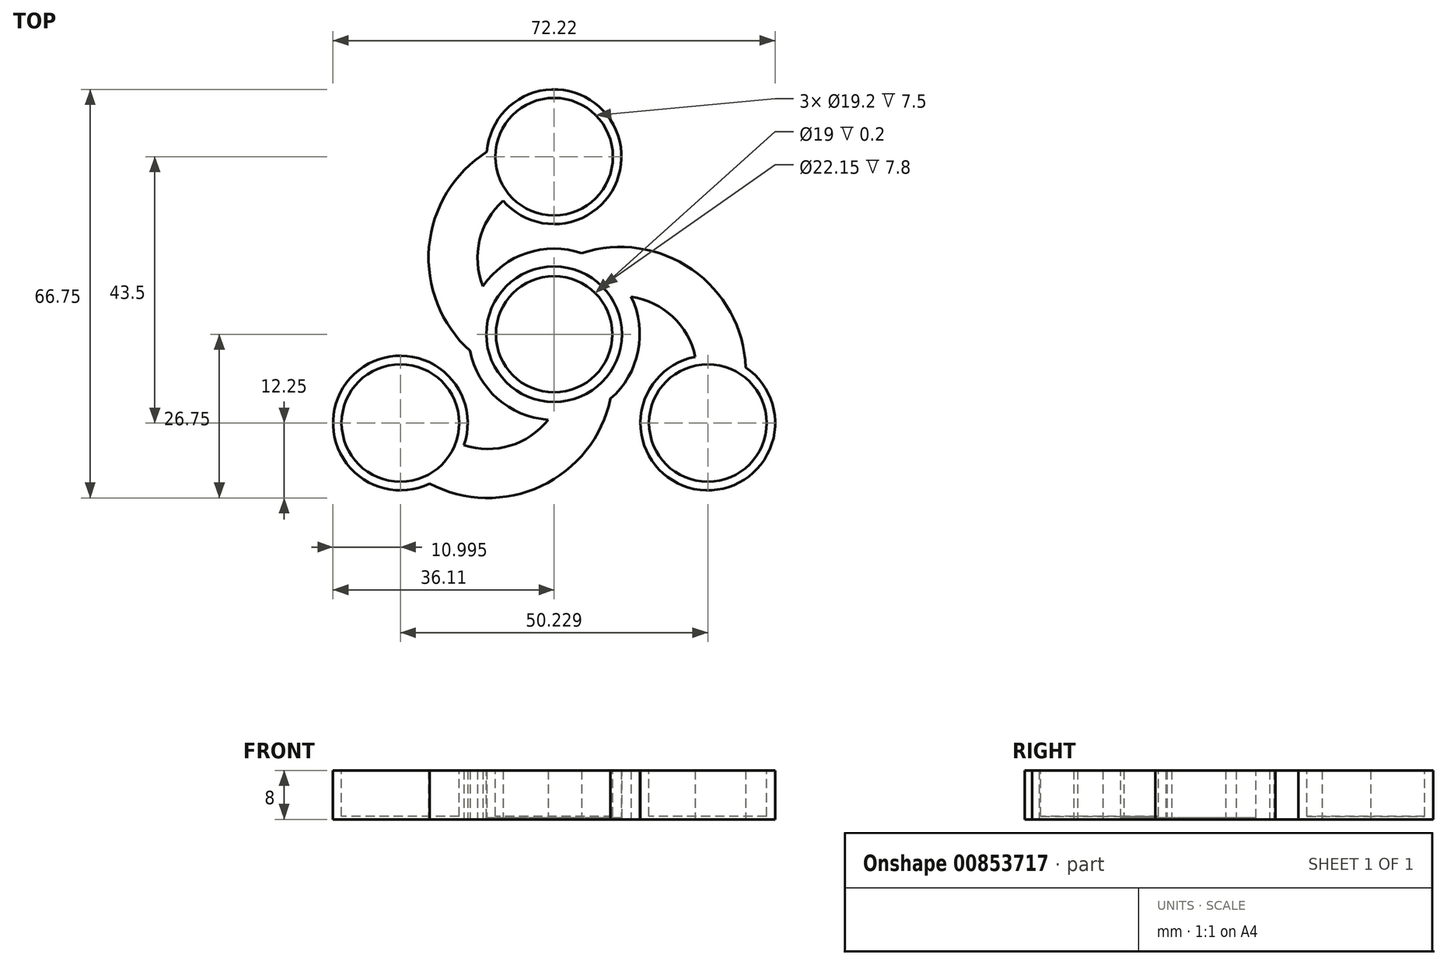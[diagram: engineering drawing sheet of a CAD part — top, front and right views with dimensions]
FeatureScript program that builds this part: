
annotation { "Feature Type Name" : "Feature", "Feature Type Description" : "" }
export const myFeature = defineFeature(function(context is Context, id is Id, definition is map)
    precondition{}
    {
        {
            var Q0;
            Q0=qCreatedBy(makeId("Top.planeOp"),FACE);
            var sketch = newSketch(context, id + "F0", { "sketchPlane" : qUnion([Q0])});
            skCircle(sketch, "E0", {"center": v(0, 0) * mm, "radius": 14 * mm});
            skLineSegment(sketch, "E1", {"start": v(0, 0) * mm, "end": v(0, 25) * mm, "construction": true});
            skArc(sketch, "E2", {"start": v(0, 25) * mm, "mid": v(-12.5, 12.5) * mm, "end": v(0, 0) * mm});
            skArc(sketch, "E3.0", {"start": v(0, 33) * mm, "mid": v(-20.5, 12.5) * mm, "end": v(0, -8) * mm});
            skLineSegment(sketch, "E4", {"start": v(0, 25) * mm, "end": v(0, 33) * mm, "construction": true});
            skCircle(sketch, "E5", {"center": v(0, 29) * mm, "radius": 11 * mm});
            skArc(sketch, "E6.1.0", {"start": v(-21.65, -12.5) * mm, "mid": v(-4.58, -17.08) * mm, "end": v(0, 0) * mm});
            skArc(sketch, "E6.1.1", {"start": v(-28.58, -16.5) * mm, "mid": v(-0.58, -24) * mm, "end": v(6.93, 4) * mm});
            skCircle(sketch, "E6.1.2", {"center": v(-25.11, -14.5) * mm, "radius": 11 * mm});
            skArc(sketch, "E6.2.0", {"start": v(21.65, -12.5) * mm, "mid": v(17.08, 4.58) * mm, "end": v(0, 0) * mm});
            skArc(sketch, "E6.2.1", {"start": v(28.58, -16.5) * mm, "mid": v(21.08, 11.5) * mm, "end": v(-6.93, 4) * mm});
            skCircle(sketch, "E6.2.2", {"center": v(25.11, -14.5) * mm, "radius": 11 * mm});
            skSolve(sketch);
        }
        {
            var Q0;
            {var subQ0=sQuery(id+"F0.wireOp",EDGE,"E6.1.1");var subQ1=sQuery(id+"F0.wireOp",EDGE,"E0");var subQ2=makeQuery(id+"F0.imprint","INTERSECT",VERTEX,{"derivedFrom":[subQ1,subQ0]});Q0=makeQuery(id+"F0.imprint","IMPRINT",FACE,{"disambiguationData":[TD([[makeQuery(id+"F0.imprint","IMPRINT",EDGE,{"disambiguationData":[TD([[subQ2,1.0]])],"derivedFrom":subQ1}),-1.0]])]});}
            var Q1;
            {var subQ0=sQuery(id+"F0.wireOp",EDGE,"E0");var subQ1=makeQuery(id+"F0.imprint","INTERSECT",VERTEX,{"derivedFrom":[subQ0,sQuery(id+"F0.wireOp",EDGE,"E6.1.1")]});Q1=makeQuery(id+"F0.imprint","IMPRINT",FACE,{"disambiguationData":[TD([[makeQuery(id+"F0.imprint","IMPRINT",EDGE,{"disambiguationData":[TD([[subQ1,1.0]])],"derivedFrom":subQ0}),1.0]])]});}
            var Q2;
            {var subQ0=sQuery(id+"F0.wireOp",EDGE,"E0");var subQ1=makeQuery(id+"F0.imprint","INTERSECT",VERTEX,{"derivedFrom":[subQ0,sQuery(id+"F0.wireOp",EDGE,"E3.0")]});Q2=makeQuery(id+"F0.imprint","IMPRINT",FACE,{"disambiguationData":[TD([[makeQuery(id+"F0.imprint","IMPRINT",EDGE,{"disambiguationData":[TD([[subQ1,1.0]])],"derivedFrom":subQ0}),1.0]])]});}
            var Q3;
            {var subQ0=sQuery(id+"F0.wireOp",EDGE,"E6.1.2");var subQ1=makeQuery(id+"F0.imprint","INTERSECT",VERTEX,{"derivedFrom":[sQuery(id+"F0.wireOp",EDGE,"E6.1.0"),subQ0]});Q3=makeQuery(id+"F0.imprint","IMPRINT",FACE,{"disambiguationData":[TD([[makeQuery(id+"F0.imprint","IMPRINT",EDGE,{"disambiguationData":[TD([[subQ1,1.0]])],"derivedFrom":subQ0}),1.0]])]});}
            var Q4;
            {var subQ0=sQuery(id+"F0.wireOp",EDGE,"E6.2.2");var subQ1=makeQuery(id+"F0.imprint","INTERSECT",VERTEX,{"derivedFrom":[sQuery(id+"F0.wireOp",EDGE,"E6.2.0"),subQ0]});Q4=makeQuery(id+"F0.imprint","IMPRINT",FACE,{"disambiguationData":[TD([[makeQuery(id+"F0.imprint","IMPRINT",EDGE,{"disambiguationData":[TD([[subQ1,1.0]])],"derivedFrom":subQ0}),1.0]])]});}
            var Q5;
            {var subQ0=sQuery(id+"F0.wireOp",EDGE,"E6.2.1");var subQ1=sQuery(id+"F0.wireOp",EDGE,"E0");var subQ2=makeQuery(id+"F0.imprint","INTERSECT",VERTEX,{"derivedFrom":[subQ1,subQ0]});Q5=makeQuery(id+"F0.imprint","IMPRINT",FACE,{"disambiguationData":[TD([[makeQuery(id+"F0.imprint","IMPRINT",EDGE,{"disambiguationData":[TD([[subQ2,1.0]])],"derivedFrom":subQ1}),-1.0]])]});}
            var Q6;
            {var subQ0=sQuery(id+"F0.wireOp",EDGE,"E0");var subQ1=makeQuery(id+"F0.imprint","INTERSECT",VERTEX,{"derivedFrom":[subQ0,sQuery(id+"F0.wireOp",EDGE,"E6.2.1")]});Q6=makeQuery(id+"F0.imprint","IMPRINT",FACE,{"disambiguationData":[TD([[makeQuery(id+"F0.imprint","IMPRINT",EDGE,{"disambiguationData":[TD([[subQ1,1.0]])],"derivedFrom":subQ0}),1.0]])]});}
            var Q7;
            {var subQ0=sQuery(id+"F0.wireOp",EDGE,"E3.0");var subQ1=sQuery(id+"F0.wireOp",EDGE,"E0");var subQ2=makeQuery(id+"F0.imprint","INTERSECT",VERTEX,{"derivedFrom":[subQ1,subQ0]});Q7=makeQuery(id+"F0.imprint","IMPRINT",FACE,{"disambiguationData":[TD([[makeQuery(id+"F0.imprint","IMPRINT",EDGE,{"disambiguationData":[TD([[subQ2,1.0]])],"derivedFrom":subQ1}),-1.0]])]});}
            var Q8;
            {var subQ0=sQuery(id+"F0.wireOp",EDGE,"E5");var subQ1=makeQuery(id+"F0.imprint","INTERSECT",VERTEX,{"derivedFrom":[sQuery(id+"F0.wireOp",EDGE,"E2"),subQ0]});Q8=makeQuery(id+"F0.imprint","IMPRINT",FACE,{"disambiguationData":[TD([[makeQuery(id+"F0.imprint","IMPRINT",EDGE,{"disambiguationData":[TD([[subQ1,1.0]])],"derivedFrom":subQ0}),1.0]])]});}
            extrude(context, id + "F1", {"entities" : qUnion([Q0, Q1, Q2, Q3, Q4, Q5, Q6, Q7, Q8]), "depth" : 8 * mm, "offsetDistance" : 25 * mm});
        }
        {
            var Q0;
            Q0=makeQuery(id+"F1.opExtrude","CAP_FACE",FACE,{"disambiguationData":[OSD([sQuery(id+"F0.wireOp",EDGE,"E0"),sQuery(id+"F0.wireOp",EDGE,"E2"),sQuery(id+"F0.wireOp",EDGE,"E3.0"),sQuery(id+"F0.wireOp",EDGE,"E5"),sQuery(id+"F0.wireOp",EDGE,"E6.1.0"),sQuery(id+"F0.wireOp",EDGE,"E6.1.1"),sQuery(id+"F0.wireOp",EDGE,"E6.1.2"),sQuery(id+"F0.wireOp",EDGE,"E6.2.0"),sQuery(id+"F0.wireOp",EDGE,"E6.2.1"),sQuery(id+"F0.wireOp",EDGE,"E6.2.2")])],"isStart":false});
            var sketch = newSketch(context, id + "F2", { "sketchPlane" : qUnion([Q0])});
            skCircle(sketch, "E7", {"center": v(0, 29) * mm, "radius": 9.6 * mm});
            skCircle(sketch, "E8.1.0", {"center": v(-25.11, -14.5) * mm, "radius": 9.6 * mm});
            skCircle(sketch, "E8.2.0", {"center": v(25.11, -14.5) * mm, "radius": 9.6 * mm});
            skPoint(sketch, "E8.center", {"position": v(0, 0) * mm});
            skSolve(sketch);
        }
        {
            var Q0;
            Q0 = qSketchRegion(id + "F2", true);
            extrude(context, id + "F3", {"entities" : qUnion([Q0]), "operationType" : NewBodyOperationType.REMOVE, "oppositeDirection" : true, "depth" : 7.5 * mm, "offsetDistance" : 25 * mm});
        }
        {
            var Q0;
            Q0=makeQuery(id+"F1.opExtrude","CAP_FACE",FACE,{"disambiguationData":[OSD([sQuery(id+"F0.wireOp",EDGE,"E0"),sQuery(id+"F0.wireOp",EDGE,"E2"),sQuery(id+"F0.wireOp",EDGE,"E3.0"),sQuery(id+"F0.wireOp",EDGE,"E5"),sQuery(id+"F0.wireOp",EDGE,"E6.1.0"),sQuery(id+"F0.wireOp",EDGE,"E6.1.1"),sQuery(id+"F0.wireOp",EDGE,"E6.1.2"),sQuery(id+"F0.wireOp",EDGE,"E6.2.0"),sQuery(id+"F0.wireOp",EDGE,"E6.2.1"),sQuery(id+"F0.wireOp",EDGE,"E6.2.2")])],"isStart":false});
            var sketch = newSketch(context, id + "F4", { "sketchPlane" : qUnion([Q0])});
            skCircle(sketch, "E9", {"center": v(0, 0) * mm, "radius": 9.5 * mm});
            skSolve(sketch);
        }
        {
            var Q0;
            Q0 = qSketchRegion(id + "F4", true);
            extrude(context, id + "F5", {"entities" : qUnion([Q0]), "operationType" : NewBodyOperationType.REMOVE, "endBound" : BoundingType.UP_TO_NEXT, "oppositeDirection" : true, "depth" : 25 * mm, "offsetDistance" : 25 * mm});
        }
        {
            var Q0;
            Q0=makeQuery(id+"F1.opExtrude","CAP_FACE",FACE,{"disambiguationData":[OSD([sQuery(id+"F0.wireOp",EDGE,"E0"),sQuery(id+"F0.wireOp",EDGE,"E2"),sQuery(id+"F0.wireOp",EDGE,"E3.0"),sQuery(id+"F0.wireOp",EDGE,"E5"),sQuery(id+"F0.wireOp",EDGE,"E6.1.0"),sQuery(id+"F0.wireOp",EDGE,"E6.1.1"),sQuery(id+"F0.wireOp",EDGE,"E6.1.2"),sQuery(id+"F0.wireOp",EDGE,"E6.2.0"),sQuery(id+"F0.wireOp",EDGE,"E6.2.1"),sQuery(id+"F0.wireOp",EDGE,"E6.2.2")])],"isStart":false});
            var sketch = newSketch(context, id + "F6", { "sketchPlane" : qUnion([Q0])});
            skCircle(sketch, "E10", {"center": v(0, 0) * mm, "radius": 11.07 * mm});
            skSolve(sketch);
        }
        {
            var Q0;
            Q0 = qSketchRegion(id + "F6", true);
            extrude(context, id + "F7", {"entities" : qUnion([Q0]), "operationType" : NewBodyOperationType.REMOVE, "oppositeDirection" : true, "depth" : 7.8 * mm, "offsetDistance" : 25 * mm});
        }
    });
